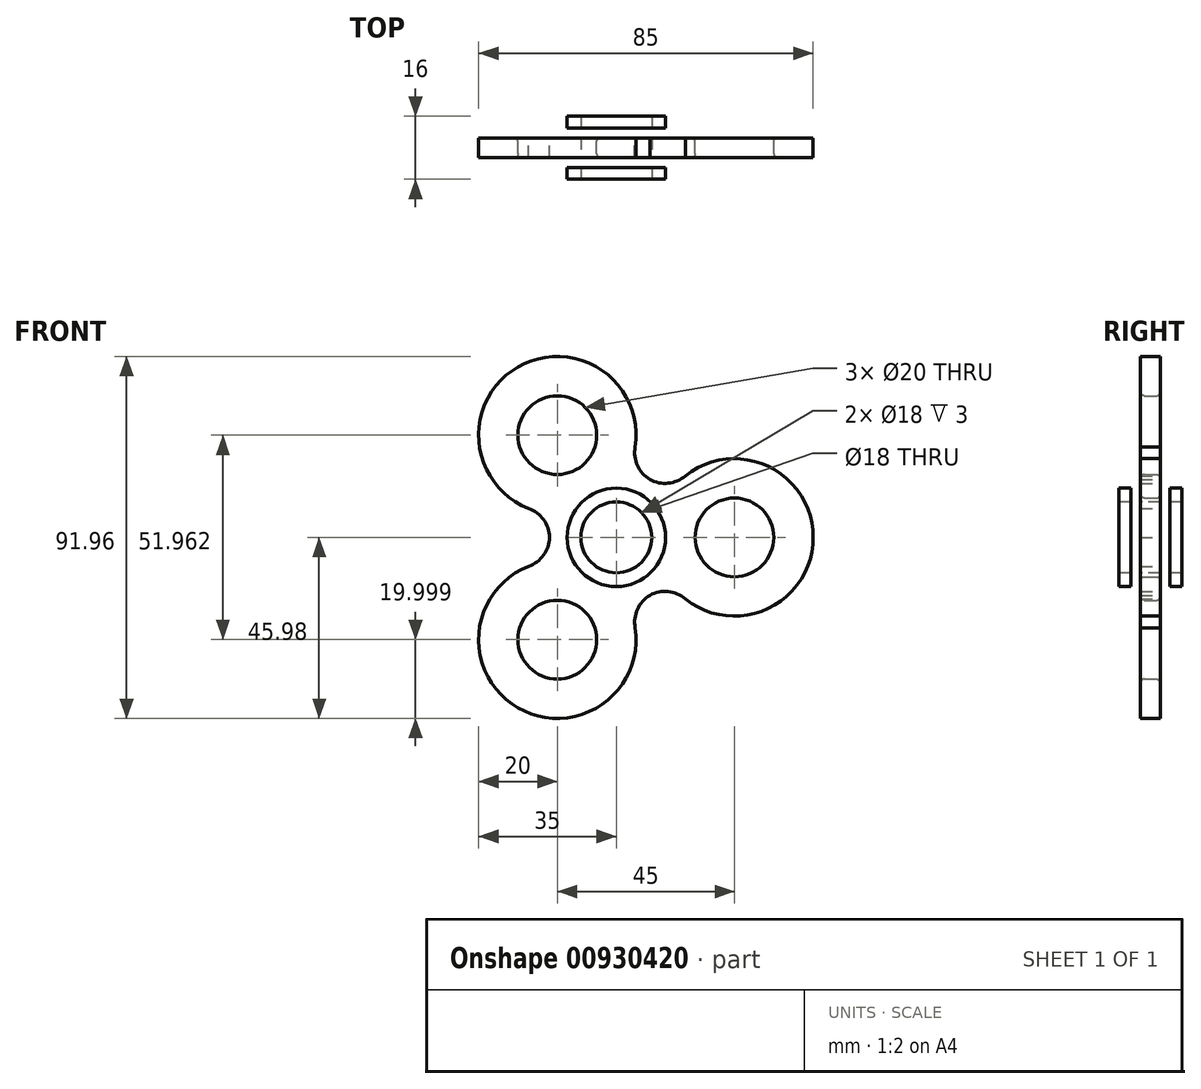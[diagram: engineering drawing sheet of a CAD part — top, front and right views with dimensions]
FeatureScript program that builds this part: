
annotation { "Feature Type Name" : "Feature", "Feature Type Description" : "" }
export const myFeature = defineFeature(function(context is Context, id is Id, definition is map)
    precondition{}
    {
        {
            var Q0;
            Q0=qCreatedBy(makeId("Front.planeOp"),FACE);
            var sketch = newSketch(context, id + "F0", { "sketchPlane" : qUnion([Q0])});
            skCircle(sketch, "E0", {"center": v(0, 0) * mm, "radius": 12.5 * mm});
            skSolve(sketch);
        }
        {
            var Q0;
            Q0 = qSketchRegion(id + "F0", true);
            extrude(context, id + "F1", {"entities" : qUnion([Q0]), "depth" : 3 * mm, "offsetDistance" : 25 * mm});
        }
        {
            var Q0;
            Q0=makeQuery(id+"F1.opExtrude","CAP_FACE",FACE,{"disambiguationData":[OSD([sQuery(id+"F0.wireOp",EDGE,"E0")])],"isStart":false});
            var sketch = newSketch(context, id + "F2", { "sketchPlane" : qUnion([Q0])});
            skCircle(sketch, "E1", {"center": v(0, 0) * mm, "radius": 4 * mm});
            skCircle(sketch, "E2", {"center": v(0, 0) * mm, "radius": 5 * mm});
            skSolve(sketch);
        }
        {
            var Q0;
            Q0 = qSketchRegion(id + "F2", true);
            extrude(context, id + "F3", {"entities" : qUnion([Q0]), "operationType" : NewBodyOperationType.ADD, "depth" : 2 * mm, "offsetDistance" : 25 * mm});
        }
        {
            var Q0;
            {var subQ0=sQuery(id+"F0.wireOp",EDGE,"E0");Q0=makeQuery(id+"F3.boolean.opBoolean","SPLIT",FACE,{"disambiguationData":[TD([makeQuery(id+"F1.opExtrude","SWEPT_FACE",FACE,{"disambiguationData":[OSD([subQ0])]})])],"derivedFrom":makeQuery(id+"F1.opExtrude","CAP_FACE",FACE,{"disambiguationData":[OSD([subQ0])],"isStart":false})});}
            var sketch = newSketch(context, id + "F4", { "sketchPlane" : qUnion([Q0])});
            skCircle(sketch, "E3", {"center": v(0, 0) * mm, "radius": 3 * mm});
            skSolve(sketch);
        }
        {
            var Q0;
            Q0 = qSketchRegion(id + "F4", true);
            extrude(context, id + "F5", {"entities" : qUnion([Q0]), "operationType" : NewBodyOperationType.ADD, "depth" : 10 * mm, "offsetDistance" : 25 * mm});
        }
        {
            var Q0;
            {var subQ0=sQuery(id+"F0.wireOp",EDGE,"E0");Q0=makeQuery(id+"F3.boolean.opBoolean","SPLIT",FACE,{"disambiguationData":[TD([makeQuery(id+"F1.opExtrude","SWEPT_FACE",FACE,{"disambiguationData":[OSD([subQ0])]})])],"derivedFrom":makeQuery(id+"F1.opExtrude","CAP_FACE",FACE,{"disambiguationData":[OSD([subQ0])],"isStart":false})});}
            cPlane(context, id + "F6", {"entities" : qUnion([Q0]), "cplaneType" : CPlaneType.OFFSET, "offset" : 0 * mm, "oppositeDirection" : true, "width" : 150 * mm, "height" : 150 * mm});
        }
        {
            var Q0;
            Q0=qCreatedBy(id+"F6.planeOp",FACE);
            var sketch = newSketch(context, id + "F7", { "sketchPlane" : qUnion([Q0])});
            skCircle(sketch, "E4", {"center": v(0, 0) * mm, "radius": 5 * mm});
            skCircle(sketch, "E5", {"center": v(0, 0) * mm, "radius": 6 * mm});
            skSolve(sketch);
        }
        {
            var Q0;
            Q0 = qSketchRegion(id + "F7", true);
            extrude(context, id + "F8", {"entities" : qUnion([Q0]), "depth" : 10 * mm, "offsetDistance" : 25 * mm});
        }
        {
            var Q0;
            Q0=qCreatedBy(id+"F6.planeOp",FACE);
            var sketch = newSketch(context, id + "F9", { "sketchPlane" : qUnion([Q0])});
            skCircle(sketch, "E6", {"center": v(0, 0) * mm, "radius": 8 * mm});
            skCircle(sketch, "E7", {"center": v(0, 0) * mm, "radius": 9 * mm});
            skSolve(sketch);
        }
        {
            var Q0;
            Q0 = qSketchRegion(id + "F9", true);
            extrude(context, id + "F10", {"entities" : qUnion([Q0]), "depth" : 10 * mm, "offsetDistance" : 25 * mm});
        }
        {
            var Q0;
            Q0=makeQuery(id+"F5.opExtrude","CAP_FACE",FACE,{"disambiguationData":[OSD([sQuery(id+"F4.wireOp",EDGE,"E3")])],"isStart":false});
            cPlane(context, id + "F11", {"entities" : qUnion([Q0]), "cplaneType" : CPlaneType.OFFSET, "offset" : 0 * mm, "width" : 150 * mm, "height" : 150 * mm});
        }
        {
            var Q0;
            Q0=qCreatedBy(id+"F11.planeOp",FACE);
            var sketch = newSketch(context, id + "F12", { "sketchPlane" : qUnion([Q0])});
            skCircle(sketch, "E8", {"center": v(0, 0) * mm, "radius": 12.5 * mm});
            skSolve(sketch);
        }
        {
            var Q0;
            Q0 = qSketchRegion(id + "F12", true);
            extrude(context, id + "F13", {"entities" : qUnion([Q0]), "operationType" : NewBodyOperationType.ADD, "depth" : 3 * mm, "offsetDistance" : 25 * mm});
        }
        {
            var Q0;
            Q0=qCreatedBy(id+"F11.planeOp",FACE);
            var sketch = newSketch(context, id + "F14", { "sketchPlane" : qUnion([Q0])});
            skCircle(sketch, "E9", {"center": v(0, 0) * mm, "radius": 4 * mm});
            skCircle(sketch, "E10", {"center": v(0, 0) * mm, "radius": 3 * mm});
            skSolve(sketch);
        }
        {
            var Q0;
            Q0 = qSketchRegion(id + "F14", true);
            extrude(context, id + "F15", {"entities" : qUnion([Q0]), "operationType" : NewBodyOperationType.ADD, "oppositeDirection" : true, "depth" : 3 * mm, "offsetDistance" : 25 * mm});
        }
        {
            var Q0;
            Q0=qCreatedBy(id+"F6.planeOp",FACE);
            cPlane(context, id + "F16", {"entities" : qUnion([Q0]), "cplaneType" : CPlaneType.OFFSET, "offset" : 5 * mm, "width" : 150 * mm, "height" : 150 * mm});
        }
        {
            var Q0;
            Q0=qCreatedBy(id+"F16.planeOp",FACE);
            var sketch = newSketch(context, id + "F17", { "sketchPlane" : qUnion([Q0])});
            skLineSegment(sketch, "E11", {"start": v(0, 0) * mm, "end": v(30, 0) * mm, "construction": true});
            skLineSegment(sketch, "E12", {"start": v(0, 0) * mm, "end": v(8.5, 14.71) * mm});
            skArc(sketch, "E13", {"start": v(8.5, 14.71) * mm, "mid": v(13.15, 13.77) * mm, "end": v(17.53, 15.63) * mm});
            skArc(sketch, "E14.MirrorCS", {"start": v(8.5, -14.71) * mm, "mid": v(13.15, -13.77) * mm, "end": v(17.53, -15.63) * mm});
            skLineSegment(sketch, "E15.MirrorCS", {"start": v(0, 0) * mm, "end": v(8.5, -14.71) * mm});
            skArc(sketch, "E16", {"start": v(17.53, 15.63) * mm, "mid": v(50, 0) * mm, "end": v(17.53, -15.63) * mm});
            skCircle(sketch, "E17", {"center": v(30, 0) * mm, "radius": 10 * mm});
            skSolve(sketch);
        }
        {
            var Q0;
            Q0 = qSketchRegion(id + "F17", true);
            extrude(context, id + "F18", {"entities" : qUnion([Q0]), "endBound" : BoundingType.SYMMETRIC, "depth" : 5 * mm, "offsetDistance" : 25 * mm});
        }
        {
            var Q0;
            Q0=makeQuery(id+"F18.opExtrude","CAP_EDGE",EDGE,{"disambiguationData":[OSD([sQuery(id+"F17.wireOp",EDGE,"E17")])],"isStart":false});
            var Q1;
            Q1=makeQuery(id+"F18.opExtrude","CAP_EDGE",EDGE,{"disambiguationData":[OSD([sQuery(id+"F17.wireOp",EDGE,"E17")])],"isStart":true});
            fillet(context, id + "F19", {"entities" : qUnion([Q0, Q1]), "radius" : 1 * mm, "tangentPropagation" : true, "allowEdgeOverflow" : false});
        }
        {
            var Q0;
            Q0=makeQuery(id+"F18.opExtrude","SWEPT_BODY",BODY,{"disambiguationData":[OSD([sQuery(id+"F17.wireOp",EDGE,"E12"),sQuery(id+"F17.wireOp",EDGE,"E13"),sQuery(id+"F17.wireOp",EDGE,"E14.MirrorCS"),sQuery(id+"F17.wireOp",EDGE,"E15.MirrorCS"),sQuery(id+"F17.wireOp",EDGE,"E16"),sQuery(id+"F17.wireOp",EDGE,"E17")])]});
            var Q1;
            Q1=makeQuery(id+"F10.opExtrude","SWEPT_FACE",FACE,{"disambiguationData":[OSD([sQuery(id+"F9.wireOp",EDGE,"E7")])]});
            circularPattern(context, id + "F20", {"operationType" : NewBodyOperationType.ADD, "entities" : qUnion([Q0]), "axis" : qUnion([Q1]), "angle" : 360 * degree, "instanceCount" : 3, "equalSpace" : true});
        }
        {
            var Q0;
            Q0=qCreatedBy(id+"F16.planeOp",FACE);
            var sketch = newSketch(context, id + "F21", { "sketchPlane" : qUnion([Q0])});
            skCircle(sketch, "E18.0.0", {"center": v(0, 0) * mm, "radius": 9 * mm});
            skSolve(sketch);
        }
        {
            var Q0;
            Q0 = qSketchRegion(id + "F21", true);
            extrude(context, id + "F22", {"entities" : qUnion([Q0]), "operationType" : NewBodyOperationType.REMOVE, "endBound" : BoundingType.SYMMETRIC, "oppositeDirection" : true, "depth" : 25 * mm, "offsetDistance" : 25 * mm});
        }
    });
